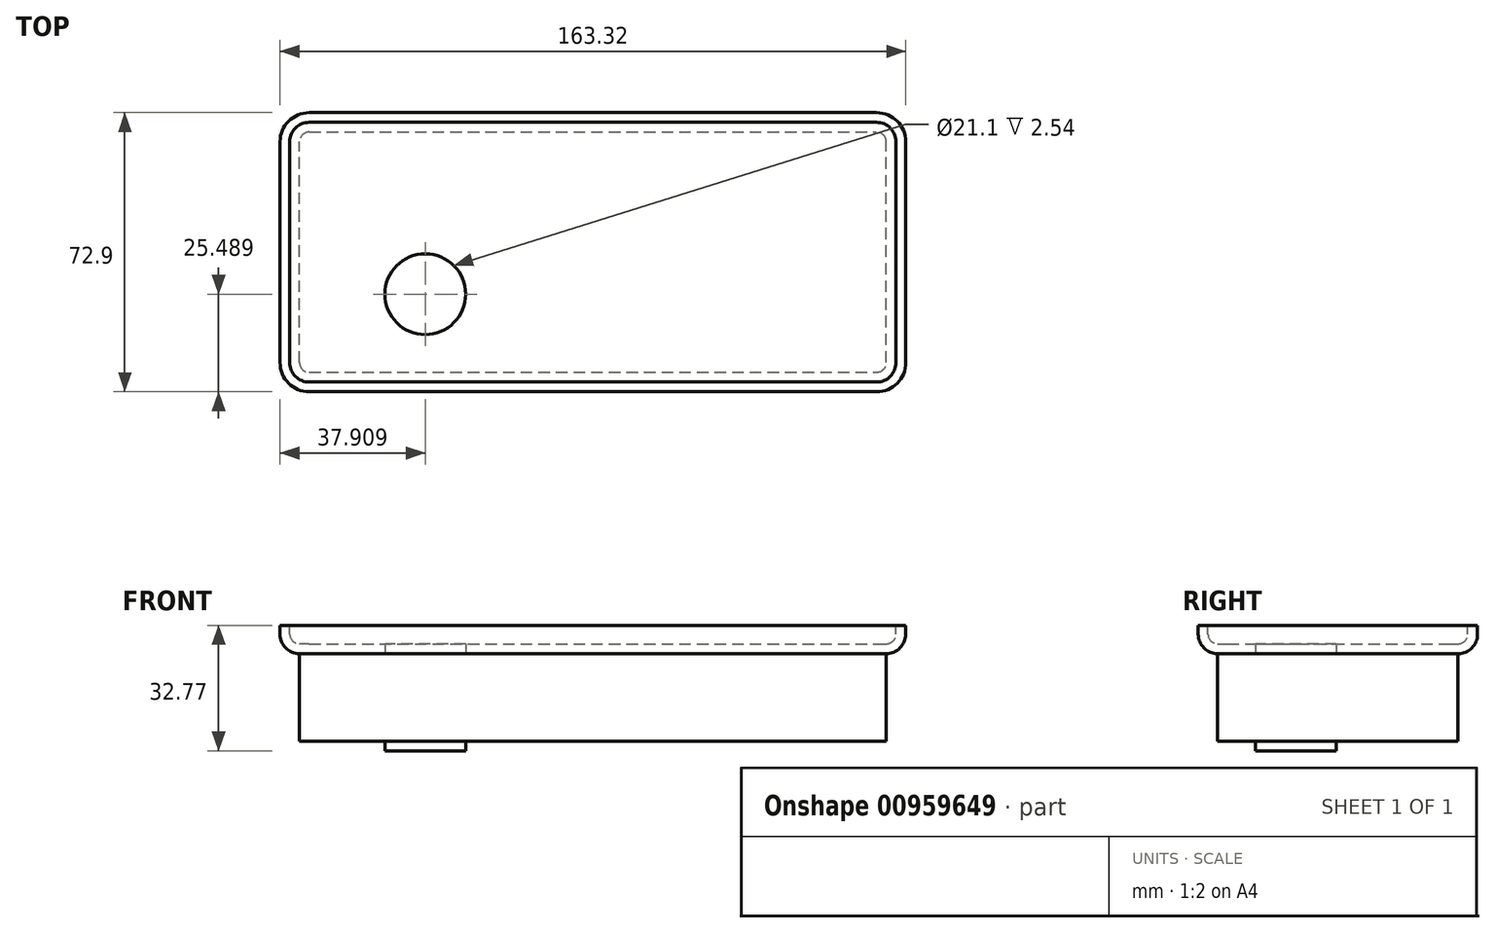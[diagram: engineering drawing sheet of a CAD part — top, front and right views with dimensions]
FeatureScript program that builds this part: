
annotation { "Feature Type Name" : "Feature", "Feature Type Description" : "" }
export const myFeature = defineFeature(function(context is Context, id is Id, definition is map)
    precondition{}
    {
        {
            var Q0;
            Q0=qCreatedBy(makeId("Top.planeOp"),FACE);
            var sketch = newSketch(context, id + "F0", { "sketchPlane" : qUnion([Q0])});
            skLineSegment(sketch, "E0.bottom", {"start": v(0, 0) * mm, "end": v(163.32, 0) * mm});
            skLineSegment(sketch, "E0.top", {"start": v(0, 72.9) * mm, "end": v(163.32, 72.9) * mm});
            skLineSegment(sketch, "E0.left", {"start": v(0, 0) * mm, "end": v(0, 72.9) * mm});
            skLineSegment(sketch, "E0.right", {"start": v(163.32, 0) * mm, "end": v(163.32, 72.9) * mm});
            skSolve(sketch);
        }
        {
            var Q0;
            Q0 = qSketchRegion(id + "F0", true);
            extrude(context, id + "F1", {"entities" : qUnion([Q0]), "depth" : 7.37 * mm, "offsetDistance" : 25.4 * mm});
        }
        {
            var Q0;
            Q0=makeQuery(id+"F1.opExtrude","SWEPT_EDGE",EDGE,{"disambiguationData":[OSD([sQuery(id+"F0.wireOp",EDGE,"E0.top"),sQuery(id+"F0.wireOp",EDGE,"E0.right")])]});
            var Q1;
            Q1=makeQuery(id+"F1.opExtrude","SWEPT_EDGE",EDGE,{"disambiguationData":[OSD([sQuery(id+"F0.wireOp",EDGE,"E0.top"),sQuery(id+"F0.wireOp",EDGE,"E0.left")])]});
            var Q2;
            Q2=makeQuery(id+"F1.opExtrude","SWEPT_EDGE",EDGE,{"disambiguationData":[OSD([sQuery(id+"F0.wireOp",EDGE,"E0.bottom"),sQuery(id+"F0.wireOp",EDGE,"E0.right")])]});
            var Q3;
            Q3=makeQuery(id+"F1.opExtrude","SWEPT_EDGE",EDGE,{"disambiguationData":[OSD([sQuery(id+"F0.wireOp",EDGE,"E0.bottom"),sQuery(id+"F0.wireOp",EDGE,"E0.left")])]});
            fillet(context, id + "F2", {"entities" : qUnion([Q0, Q1, Q2, Q3]), "radius" : 7.62 * mm, "tangentPropagation" : true, "allowEdgeOverflow" : false});
        }
        {
            var Q0;
            Q0=makeQuery(id+"F1.opExtrude","CAP_FACE",FACE,{"disambiguationData":[OSD([sQuery(id+"F0.wireOp",EDGE,"E0.bottom"),sQuery(id+"F0.wireOp",EDGE,"E0.top"),sQuery(id+"F0.wireOp",EDGE,"E0.left"),sQuery(id+"F0.wireOp",EDGE,"E0.right")])],"isStart":true});
            fillet(context, id + "F3", {"entities" : qUnion([Q0]), "radius" : 5.08 * mm, "tangentPropagation" : true, "allowEdgeOverflow" : false});
        }
        {
            var Q0;
            Q0=makeQuery(id+"F1.opExtrude","CAP_FACE",FACE,{"disambiguationData":[OSD([sQuery(id+"F0.wireOp",EDGE,"E0.bottom"),sQuery(id+"F0.wireOp",EDGE,"E0.top"),sQuery(id+"F0.wireOp",EDGE,"E0.left"),sQuery(id+"F0.wireOp",EDGE,"E0.right")])],"isStart":false});
            shell(context, id + "F4", {"entities" : qUnion([Q0]), "thickness" : 2.54 * mm});
        }
        {
            var Q0;
            Q0=qCreatedBy(makeId("Top.planeOp"),FACE);
            var sketch = newSketch(context, id + "F5", { "sketchPlane" : qUnion([Q0])});
            skCircle(sketch, "E1", {"center": v(37.9, 25.49) * mm, "radius": 10.55 * mm});
            skSolve(sketch);
        }
        {
            var Q0;
            Q0=makeQuery(id+"F5.imprint","IMPRINT",FACE,{"disambiguationData":[TD([[makeQuery(id+"F5.imprint","IMPRINT",EDGE,{"derivedFrom":sQuery(id+"F5.wireOp",EDGE,"E1")}),1.0]])]});
            extrude(context, id + "F6", {"entities" : qUnion([Q0]), "operationType" : NewBodyOperationType.REMOVE, "depth" : 30.48 * mm, "offsetDistance" : 25.4 * mm});
        }
        {
            var Q0;
            Q0 = qSketchRegion(id + "F5", true);
            var Q1;
            {var subQ0=sQuery(id+"F0.wireOp",EDGE,"E0.right");var subQ1=sQuery(id+"F0.wireOp",EDGE,"E0.left");var subQ2=sQuery(id+"F0.wireOp",EDGE,"E0.top");var subQ3=sQuery(id+"F0.wireOp",EDGE,"E0.bottom");Q1=makeQuery(id+"F4.opShell","OFFSET_FACE",FACE,{"disambiguationData":[OSD([subQ3,subQ2,subQ1,subQ0]),TDD([makeQuery(id+"F1.opExtrude","CAP_FACE",FACE,{"disambiguationData":[OSD([subQ3,subQ2,subQ1,subQ0])],"isStart":true})])]});}
            extrude(context, id + "F7", {"entities" : qUnion([Q0, Q1]), "operationType" : NewBodyOperationType.ADD, "oppositeDirection" : true, "depth" : 25.4 * mm, "offsetDistance" : 25.4 * mm});
        }
    });
